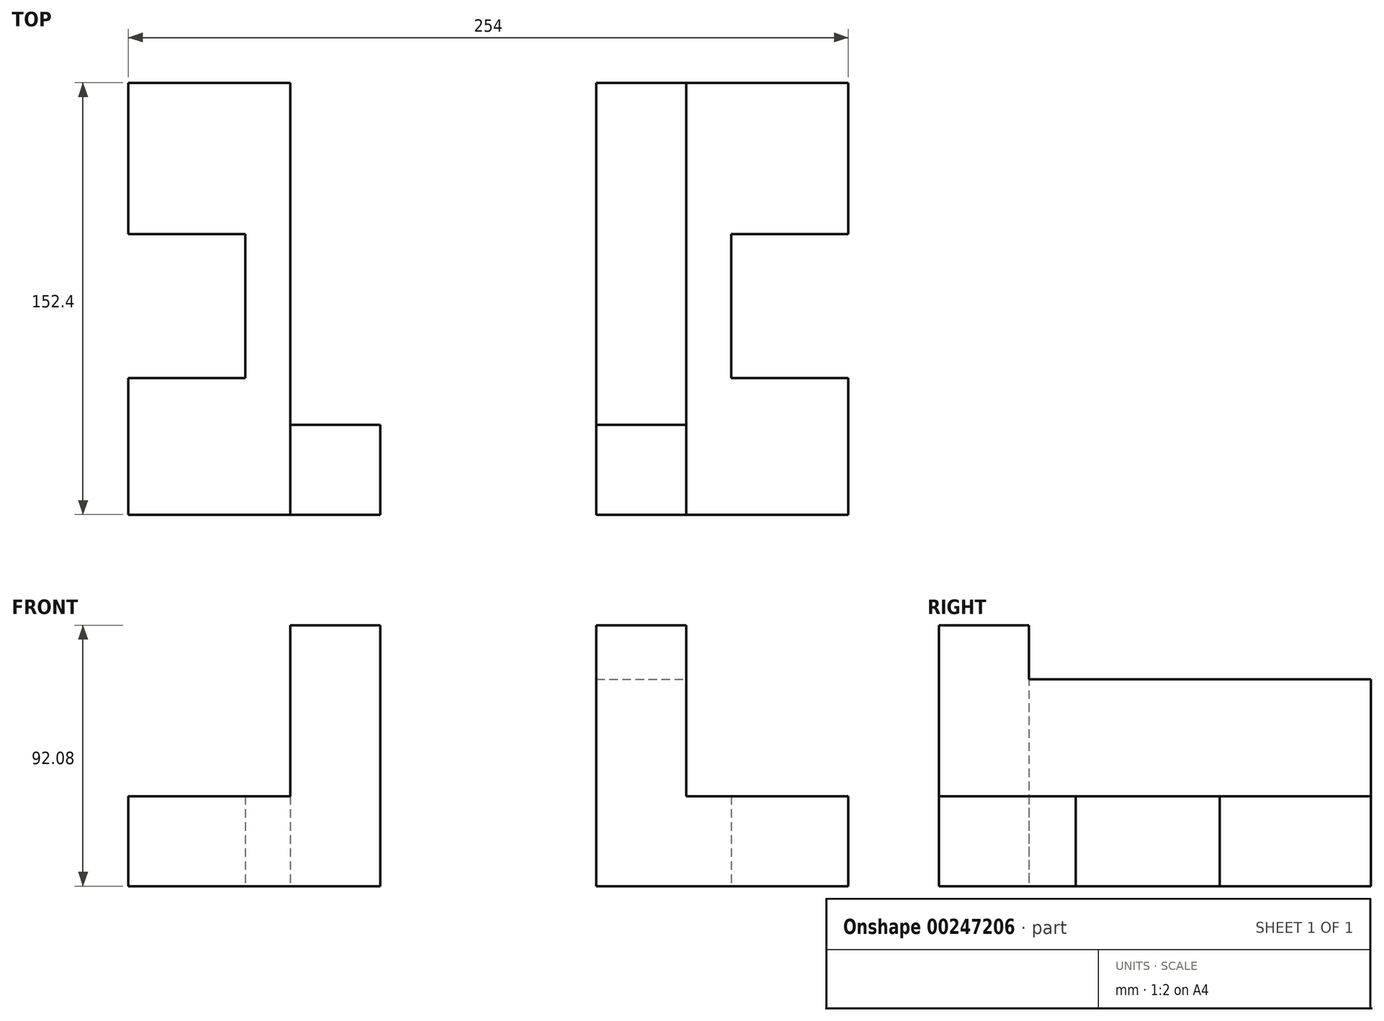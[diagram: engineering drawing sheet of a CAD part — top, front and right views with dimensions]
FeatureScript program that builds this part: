
annotation { "Feature Type Name" : "Feature", "Feature Type Description" : "" }
export const myFeature = defineFeature(function(context is Context, id is Id, definition is map)
    precondition{}
    {
        {
            var Q0;
            Q0=qCreatedBy(makeId("Top.planeOp"),FACE);
            var sketch = newSketch(context, id + "F0", { "sketchPlane" : qUnion([Q0])});
            skLineSegment(sketch, "E0.bottom", {"start": v(-75.42, 104.2) * mm, "end": v(178.58, 104.2) * mm});
            skLineSegment(sketch, "E0.top", {"start": v(-75.42, -48.2) * mm, "end": v(178.58, -48.2) * mm});
            skLineSegment(sketch, "E0.left", {"start": v(-75.42, 104.2) * mm, "end": v(-75.42, 50.8) * mm});
            skLineSegment(sketch, "E0.right", {"start": v(178.58, 104.2) * mm, "end": v(178.58, 50.8) * mm});
            skLineSegment(sketch, "E1.bottom", {"start": v(-75.42, 50.8) * mm, "end": v(-34.15, 50.8) * mm});
            skLineSegment(sketch, "E1.top", {"start": v(-75.42, 0) * mm, "end": v(-34.15, 0) * mm});
            skLineSegment(sketch, "E1.right", {"start": v(-34.15, 50.8) * mm, "end": v(-34.15, 0) * mm});
            skLineSegment(sketch, "E2.bottom", {"start": v(137.3, 50.8) * mm, "end": v(178.58, 50.8) * mm});
            skLineSegment(sketch, "E2.top", {"start": v(137.3, 0) * mm, "end": v(178.58, 0) * mm});
            skLineSegment(sketch, "E2.left", {"start": v(137.3, 50.8) * mm, "end": v(137.3, 0) * mm});
            skLineSegment(sketch, "E3.bottom", {"start": v(-18.27, 104.2) * mm, "end": v(121.43, 104.2) * mm});
            skLineSegment(sketch, "E3.top", {"start": v(-18.27, -48.2) * mm, "end": v(121.43, -48.2) * mm});
            skLineSegment(sketch, "E3.left", {"start": v(-18.27, 104.2) * mm, "end": v(-18.27, -48.2) * mm});
            skLineSegment(sketch, "E3.right", {"start": v(121.43, 104.2) * mm, "end": v(121.43, -48.2) * mm});
            skLineSegment(sketch, "E4.bottom", {"start": v(-18.27, 104.2) * mm, "end": v(13.48, 104.2) * mm});
            skLineSegment(sketch, "E4.top", {"start": v(-18.27, -48.2) * mm, "end": v(13.48, -48.2) * mm});
            skLineSegment(sketch, "E4.right", {"start": v(13.48, 104.2) * mm, "end": v(13.48, -48.2) * mm});
            skLineSegment(sketch, "E5.bottom", {"start": v(89.68, 104.2) * mm, "end": v(121.43, 104.2) * mm});
            skLineSegment(sketch, "E5.top", {"start": v(89.68, -48.2) * mm, "end": v(121.43, -48.2) * mm});
            skLineSegment(sketch, "E5.left", {"start": v(89.68, 104.2) * mm, "end": v(89.68, -48.2) * mm});
            skLineSegment(sketch, "E6.top", {"start": v(-18.27, 72.45) * mm, "end": v(13.48, 72.45) * mm});
            skLineSegment(sketch, "E6.left", {"start": v(-18.27, 104.2) * mm, "end": v(-18.27, 72.45) * mm});
            skLineSegment(sketch, "E6.right", {"start": v(13.48, 104.2) * mm, "end": v(13.48, 72.45) * mm});
            skLineSegment(sketch, "E7.bottom", {"start": v(-18.27, -16.45) * mm, "end": v(13.48, -16.45) * mm});
            skLineSegment(sketch, "E7.left", {"start": v(-18.27, -16.45) * mm, "end": v(-18.27, -48.2) * mm});
            skLineSegment(sketch, "E7.right", {"start": v(13.48, -16.45) * mm, "end": v(13.48, -48.2) * mm});
            skLineSegment(sketch, "E8.top", {"start": v(89.68, 72.45) * mm, "end": v(121.43, 72.45) * mm});
            skLineSegment(sketch, "E8.left", {"start": v(89.68, 104.2) * mm, "end": v(89.68, 72.45) * mm});
            skLineSegment(sketch, "E8.right", {"start": v(121.43, 104.2) * mm, "end": v(121.43, 72.45) * mm});
            skLineSegment(sketch, "E9.bottom", {"start": v(89.68, -16.45) * mm, "end": v(121.43, -16.45) * mm});
            skLineSegment(sketch, "E9.left", {"start": v(89.68, -16.45) * mm, "end": v(89.68, -48.2) * mm});
            skLineSegment(sketch, "E9.right", {"start": v(121.43, -16.45) * mm, "end": v(121.43, -48.2) * mm});
            skCircle(sketch, "E10", {"center": v(51.58, 28) * mm, "radius": 15.88 * mm});
            skPoint(sketch, "E10.centerSnap1", {"position": v(51.58, -48.2) * mm});
            skLineSegment(sketch, "E11.trimOffspring", {"start": v(-75.42, 0) * mm, "end": v(-75.42, -48.2) * mm});
            skLineSegment(sketch, "E12.trimOffspring", {"start": v(178.58, 0) * mm, "end": v(178.58, -48.2) * mm});
            skSolve(sketch);
        }
        {
            var Q0;
            Q0=makeQuery(id+"F0.imprint","IMPRINT",FACE,{"disambiguationData":[TD([[makeQuery(id+"F0.imprint","IMPRINT",EDGE,{"derivedFrom":sQuery(id+"F0.wireOp",EDGE,"E3.bottom")}),-1.0]])]});
            var Q1;
            Q1=makeQuery(id+"F0.imprint","IMPRINT",FACE,{"disambiguationData":[TD([[makeQuery(id+"F0.imprint","IMPRINT",EDGE,{"derivedFrom":sQuery(id+"F0.wireOp",EDGE,"E5.left")}),1.0]])]});
            var Q2;
            {var subQ2=sQuery(id+"F0.wireOp",EDGE,"E0.right");Q2=makeQuery(id+"F0.imprint","IMPRINT",FACE,{"disambiguationData":[TD([[makeQuery(id+"F0.imprint","IMPRINT",EDGE,{"derivedFrom":subQ2}),-1.0]])]});}
            var Q3;
            {var subQ1=sQuery(id+"F0.wireOp",EDGE,"E0.left");Q3=makeQuery(id+"F0.imprint","IMPRINT",FACE,{"disambiguationData":[TD([[makeQuery(id+"F0.imprint","IMPRINT",EDGE,{"derivedFrom":subQ1}),1.0]])]});}
            var Q4;
            Q4=makeQuery(id+"F0.imprint","IMPRINT",FACE,{"disambiguationData":[TD([[makeQuery(id+"F0.imprint","IMPRINT",EDGE,{"derivedFrom":sQuery(id+"F0.wireOp",EDGE,"E4.bottom")}),-1.0]])]});
            var Q5;
            Q5=makeQuery(id+"F0.imprint","IMPRINT",FACE,{"disambiguationData":[TD([[makeQuery(id+"F0.imprint","IMPRINT",EDGE,{"derivedFrom":sQuery(id+"F0.wireOp",EDGE,"E5.bottom")}),-1.0]])]});
            var Q6;
            Q6=makeQuery(id+"F0.imprint","IMPRINT",FACE,{"disambiguationData":[TD([[makeQuery(id+"F0.imprint","IMPRINT",EDGE,{"derivedFrom":sQuery(id+"F0.wireOp",EDGE,"E9.bottom")}),-1.0]])]});
            var Q7;
            Q7=makeQuery(id+"F0.imprint","IMPRINT",FACE,{"disambiguationData":[TD([[makeQuery(id+"F0.imprint","IMPRINT",EDGE,{"derivedFrom":sQuery(id+"F0.wireOp",EDGE,"E7.bottom")}),-1.0]])]});
            var Q8;
            Q8=makeQuery(id+"F0.imprint","IMPRINT",FACE,{"disambiguationData":[TD([[makeQuery(id+"F0.imprint","IMPRINT",EDGE,{"derivedFrom":sQuery(id+"F0.wireOp",EDGE,"E3.left")}),1.0]])]});
            extrude(context, id + "F1", {"entities" : qUnion([Q0, Q1, Q2, Q3, Q4, Q5, Q6, Q7, Q8]), "depth" : 31.75 * mm});
        }
        {
            var Q0;
            Q0=makeQuery(id+"F0.imprint","IMPRINT",FACE,{"disambiguationData":[TD([[makeQuery(id+"F0.imprint","IMPRINT",EDGE,{"derivedFrom":sQuery(id+"F0.wireOp",EDGE,"E4.bottom")}),-1.0]])]});
            var Q1;
            Q1=makeQuery(id+"F0.imprint","IMPRINT",FACE,{"disambiguationData":[TD([[makeQuery(id+"F0.imprint","IMPRINT",EDGE,{"derivedFrom":sQuery(id+"F0.wireOp",EDGE,"E3.left")}),1.0]])]});
            var Q2;
            Q2=makeQuery(id+"F0.imprint","IMPRINT",FACE,{"disambiguationData":[TD([[makeQuery(id+"F0.imprint","IMPRINT",EDGE,{"derivedFrom":sQuery(id+"F0.wireOp",EDGE,"E7.bottom")}),-1.0]])]});
            var Q3;
            Q3=makeQuery(id+"F0.imprint","IMPRINT",FACE,{"disambiguationData":[TD([[makeQuery(id+"F0.imprint","IMPRINT",EDGE,{"derivedFrom":sQuery(id+"F0.wireOp",EDGE,"E3.bottom")}),-1.0]])]});
            var Q4;
            Q4=makeQuery(id+"F0.imprint","IMPRINT",FACE,{"disambiguationData":[TD([[makeQuery(id+"F0.imprint","IMPRINT",EDGE,{"derivedFrom":sQuery(id+"F0.wireOp",EDGE,"E9.bottom")}),-1.0]])]});
            var Q5;
            Q5=makeQuery(id+"F0.imprint","IMPRINT",FACE,{"disambiguationData":[TD([[makeQuery(id+"F0.imprint","IMPRINT",EDGE,{"derivedFrom":sQuery(id+"F0.wireOp",EDGE,"E5.left")}),1.0]])]});
            var Q6;
            Q6=makeQuery(id+"F0.imprint","IMPRINT",FACE,{"disambiguationData":[TD([[makeQuery(id+"F0.imprint","IMPRINT",EDGE,{"derivedFrom":sQuery(id+"F0.wireOp",EDGE,"E5.bottom")}),-1.0]])]});
            extrude(context, id + "F2", {"entities" : qUnion([Q0, Q1, Q2, Q3, Q4, Q5, Q6]), "operationType" : NewBodyOperationType.ADD, "depth" : 53.97 * mm});
        }
        {
            var Q0;
            Q0=makeQuery(id+"F0.imprint","IMPRINT",FACE,{"disambiguationData":[TD([[makeQuery(id+"F0.imprint","IMPRINT",EDGE,{"derivedFrom":sQuery(id+"F0.wireOp",EDGE,"E4.bottom")}),-1.0]])]});
            var Q1;
            Q1=makeQuery(id+"F0.imprint","IMPRINT",FACE,{"disambiguationData":[TD([[makeQuery(id+"F0.imprint","IMPRINT",EDGE,{"derivedFrom":sQuery(id+"F0.wireOp",EDGE,"E3.left")}),1.0]])]});
            var Q2;
            Q2=makeQuery(id+"F0.imprint","IMPRINT",FACE,{"disambiguationData":[TD([[makeQuery(id+"F0.imprint","IMPRINT",EDGE,{"derivedFrom":sQuery(id+"F0.wireOp",EDGE,"E7.bottom")}),-1.0]])]});
            var Q3;
            Q3=makeQuery(id+"F0.imprint","IMPRINT",FACE,{"disambiguationData":[TD([[makeQuery(id+"F0.imprint","IMPRINT",EDGE,{"derivedFrom":sQuery(id+"F0.wireOp",EDGE,"E9.bottom")}),-1.0]])]});
            var Q4;
            Q4=makeQuery(id+"F0.imprint","IMPRINT",FACE,{"disambiguationData":[TD([[makeQuery(id+"F0.imprint","IMPRINT",EDGE,{"derivedFrom":sQuery(id+"F0.wireOp",EDGE,"E5.left")}),1.0]])]});
            var Q5;
            Q5=makeQuery(id+"F0.imprint","IMPRINT",FACE,{"disambiguationData":[TD([[makeQuery(id+"F0.imprint","IMPRINT",EDGE,{"derivedFrom":sQuery(id+"F0.wireOp",EDGE,"E5.bottom")}),-1.0]])]});
            extrude(context, id + "F3", {"entities" : qUnion([Q0, Q1, Q2, Q3, Q4, Q5]), "operationType" : NewBodyOperationType.ADD, "depth" : 73.02 * mm});
        }
        {
            var Q0;
            Q0=makeQuery(id+"F0.imprint","IMPRINT",FACE,{"disambiguationData":[TD([[makeQuery(id+"F0.imprint","IMPRINT",EDGE,{"derivedFrom":sQuery(id+"F0.wireOp",EDGE,"E9.bottom")}),-1.0]])]});
            var Q1;
            Q1=makeQuery(id+"F0.imprint","IMPRINT",FACE,{"disambiguationData":[TD([[makeQuery(id+"F0.imprint","IMPRINT",EDGE,{"derivedFrom":sQuery(id+"F0.wireOp",EDGE,"E7.bottom")}),-1.0]])]});
            var Q2;
            Q2=makeQuery(id+"F0.imprint","IMPRINT",FACE,{"disambiguationData":[TD([[makeQuery(id+"F0.imprint","IMPRINT",EDGE,{"derivedFrom":sQuery(id+"F0.wireOp",EDGE,"E4.bottom")}),-1.0]])]});
            var Q3;
            Q3=makeQuery(id+"F0.imprint","IMPRINT",FACE,{"disambiguationData":[TD([[makeQuery(id+"F0.imprint","IMPRINT",EDGE,{"derivedFrom":sQuery(id+"F0.wireOp",EDGE,"E5.bottom")}),-1.0]])]});
            extrude(context, id + "F4", {"entities" : qUnion([Q0, Q1, Q2, Q3]), "operationType" : NewBodyOperationType.ADD, "depth" : 92.07 * mm});
        }
    });
